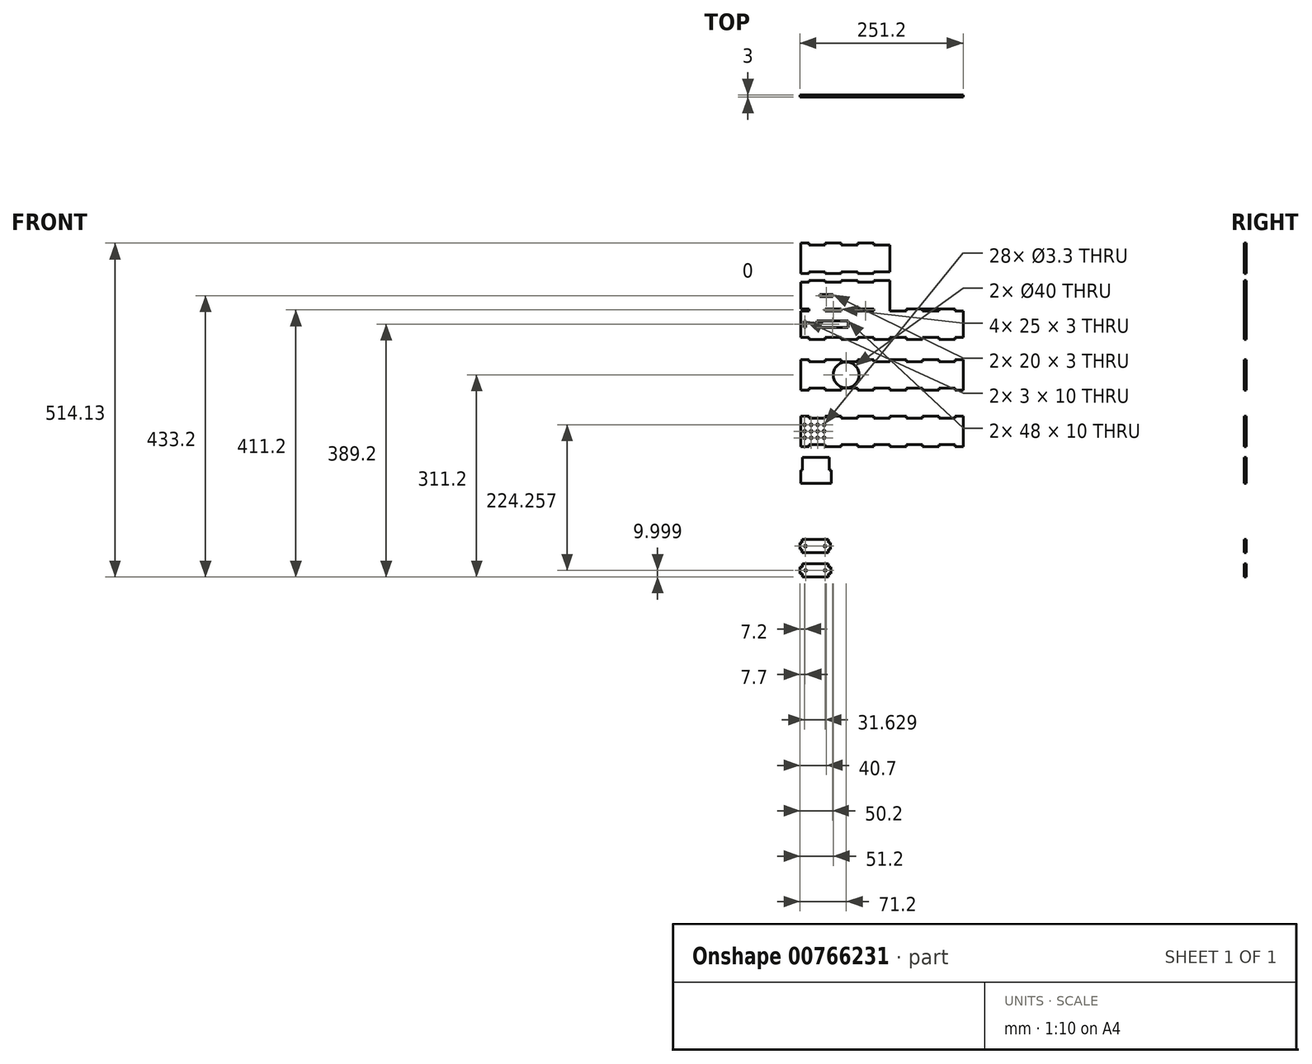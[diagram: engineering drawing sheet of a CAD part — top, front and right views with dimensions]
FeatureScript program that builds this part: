
annotation { "Feature Type Name" : "Feature", "Feature Type Description" : "" }
export const myFeature = defineFeature(function(context is Context, id is Id, definition is map)
    precondition{}
    {
        {
            var Q0;
            Q0=qCreatedBy(makeId("Front.planeOp"),FACE);
            var sketch = newSketch(context, id + "F0", { "sketchPlane" : qUnion([Q0])});
            skLineSegment(sketch, "E0.bottom", {"start": v(-125, 23.5) * mm, "end": v(-112.5, 23.5) * mm});
            skLineSegment(sketch, "E0.top", {"start": v(-125, -23.5) * mm, "end": v(-112.5, -23.5) * mm});
            skLineSegment(sketch, "E0.left", {"start": v(-125, 23.5) * mm, "end": v(-125, -23.5) * mm});
            skLineSegment(sketch, "E0.right", {"start": v(125, 23.5) * mm, "end": v(125, -23.5) * mm});
            skPoint(sketch, "E0.middle", {"position": v(0, 0) * mm});
            skLineSegment(sketch, "E1", {"start": v(-112.5, 23.5) * mm, "end": v(-112.5, 20.5) * mm});
            skLineSegment(sketch, "E2", {"start": v(-112.5, 20.5) * mm, "end": v(-87.5, 20.5) * mm});
            skLineSegment(sketch, "E3", {"start": v(-87.5, 20.5) * mm, "end": v(-87.5, 23.5) * mm});
            skLineSegment(sketch, "E4.1.0.0", {"start": v(-62.5, 23.5) * mm, "end": v(-62.5, 20.5) * mm});
            skLineSegment(sketch, "E4.1.0.1", {"start": v(-62.5, 20.5) * mm, "end": v(-37.5, 20.5) * mm});
            skLineSegment(sketch, "E4.1.0.2", {"start": v(-37.5, 20.5) * mm, "end": v(-37.5, 23.5) * mm});
            skLineSegment(sketch, "E4.2.0.0", {"start": v(-12.5, 23.5) * mm, "end": v(-12.5, 20.5) * mm});
            skLineSegment(sketch, "E4.2.0.1", {"start": v(-12.5, 20.5) * mm, "end": v(12.5, 20.5) * mm});
            skLineSegment(sketch, "E4.2.0.2", {"start": v(12.5, 20.5) * mm, "end": v(12.5, 23.5) * mm});
            skLineSegment(sketch, "E4.3.0.0", {"start": v(37.5, 23.5) * mm, "end": v(37.5, 20.5) * mm});
            skLineSegment(sketch, "E4.3.0.1", {"start": v(37.5, 20.5) * mm, "end": v(62.5, 20.5) * mm});
            skLineSegment(sketch, "E4.3.0.2", {"start": v(62.5, 20.5) * mm, "end": v(62.5, 23.5) * mm});
            skLineSegment(sketch, "E4.4.0.0", {"start": v(87.5, 23.5) * mm, "end": v(87.5, 20.5) * mm});
            skLineSegment(sketch, "E4.4.0.1", {"start": v(87.5, 20.5) * mm, "end": v(112.5, 20.5) * mm});
            skLineSegment(sketch, "E4.4.0.2", {"start": v(112.5, 20.5) * mm, "end": v(112.5, 23.5) * mm});
            skLineSegment(sketch, "E4.direction1", {"start": v(-112.5, 20.5) * mm, "end": v(-62.5, 20.5) * mm, "construction": true});
            skLineSegment(sketch, "E5.trimOffspring", {"start": v(-87.5, 23.5) * mm, "end": v(-62.5, 23.5) * mm});
            skLineSegment(sketch, "E6.trimOffspring", {"start": v(-37.5, 23.5) * mm, "end": v(-12.5, 23.5) * mm});
            skLineSegment(sketch, "E7.trimOffspring", {"start": v(12.5, 23.5) * mm, "end": v(37.5, 23.5) * mm});
            skLineSegment(sketch, "E8.trimOffspring", {"start": v(62.5, 23.5) * mm, "end": v(87.5, 23.5) * mm});
            skLineSegment(sketch, "E9.trimOffspring", {"start": v(112.5, 23.5) * mm, "end": v(125, 23.5) * mm});
            skLineSegment(sketch, "E10", {"start": v(-112.5, -23.5) * mm, "end": v(-112.5, -20.5) * mm});
            skLineSegment(sketch, "E11", {"start": v(-112.5, -20.5) * mm, "end": v(-87.5, -20.5) * mm});
            skLineSegment(sketch, "E12", {"start": v(-87.5, -20.5) * mm, "end": v(-87.5, -23.5) * mm});
            skLineSegment(sketch, "E13.1.0.0", {"start": v(-62.5, -23.5) * mm, "end": v(-62.5, -20.5) * mm});
            skLineSegment(sketch, "E13.1.0.1", {"start": v(-62.5, -20.5) * mm, "end": v(-37.5, -20.5) * mm});
            skLineSegment(sketch, "E13.1.0.2", {"start": v(-37.5, -20.5) * mm, "end": v(-37.5, -23.5) * mm});
            skLineSegment(sketch, "E13.2.0.0", {"start": v(-12.5, -23.5) * mm, "end": v(-12.5, -20.5) * mm});
            skLineSegment(sketch, "E13.2.0.1", {"start": v(-12.5, -20.5) * mm, "end": v(12.5, -20.5) * mm});
            skLineSegment(sketch, "E13.2.0.2", {"start": v(12.5, -20.5) * mm, "end": v(12.5, -23.5) * mm});
            skLineSegment(sketch, "E13.3.0.0", {"start": v(37.5, -23.5) * mm, "end": v(37.5, -20.5) * mm});
            skLineSegment(sketch, "E13.3.0.1", {"start": v(37.5, -20.5) * mm, "end": v(62.5, -20.5) * mm});
            skLineSegment(sketch, "E13.3.0.2", {"start": v(62.5, -20.5) * mm, "end": v(62.5, -23.5) * mm});
            skLineSegment(sketch, "E13.4.0.0", {"start": v(87.5, -23.5) * mm, "end": v(87.5, -20.5) * mm});
            skLineSegment(sketch, "E13.4.0.1", {"start": v(87.5, -20.5) * mm, "end": v(112.5, -20.5) * mm});
            skLineSegment(sketch, "E13.4.0.2", {"start": v(112.5, -20.5) * mm, "end": v(112.5, -23.5) * mm});
            skLineSegment(sketch, "E13.direction1", {"start": v(-87.5, -23.5) * mm, "end": v(-62.5, -23.5) * mm, "construction": true});
            skLineSegment(sketch, "E14.trimOffspring", {"start": v(-37.5, -23.5) * mm, "end": v(-12.5, -23.5) * mm});
            skLineSegment(sketch, "E15.trimOffspring", {"start": v(-87.5, -23.5) * mm, "end": v(-62.5, -23.5) * mm});
            skLineSegment(sketch, "E16.trimOffspring", {"start": v(62.5, -23.5) * mm, "end": v(87.5, -23.5) * mm});
            skLineSegment(sketch, "E17.trimOffspring", {"start": v(12.5, -23.5) * mm, "end": v(37.5, -23.5) * mm});
            skLineSegment(sketch, "E18.trimOffspring", {"start": v(112.5, -23.5) * mm, "end": v(125, -23.5) * mm});
            skLineSegment(sketch, "E19.bottom", {"start": v(-112.5, 145.5) * mm, "end": v(-87.5, 145.5) * mm});
            skLineSegment(sketch, "E19.top", {"start": v(-112.5, 54.5) * mm, "end": v(-87.5, 54.5) * mm});
            skLineSegment(sketch, "E19.left", {"start": v(-125, 142.5) * mm, "end": v(-125, 101.5) * mm});
            skPoint(sketch, "E19.middle", {"position": v(0, 100) * mm});
            skLineSegment(sketch, "E20", {"start": v(-125, 57.5) * mm, "end": v(-112.5, 57.5) * mm});
            skLineSegment(sketch, "E21", {"start": v(-112.5, 57.5) * mm, "end": v(-112.5, 54.5) * mm});
            skLineSegment(sketch, "E22", {"start": v(-87.5, 54.5) * mm, "end": v(-87.5, 57.5) * mm});
            skLineSegment(sketch, "E23", {"start": v(-87.5, 57.5) * mm, "end": v(-62.5, 57.5) * mm});
            skLineSegment(sketch, "E24", {"start": v(-62.5, 57.5) * mm, "end": v(-62.5, 54.5) * mm});
            skLineSegment(sketch, "E25.1.0.0", {"start": v(-37.5, 54.5) * mm, "end": v(-37.5, 57.5) * mm});
            skLineSegment(sketch, "E25.1.0.1", {"start": v(-37.5, 57.5) * mm, "end": v(-12.5, 57.5) * mm});
            skLineSegment(sketch, "E25.1.0.2", {"start": v(-12.5, 57.5) * mm, "end": v(-12.5, 54.5) * mm});
            skLineSegment(sketch, "E25.2.0.0", {"start": v(12.5, 54.5) * mm, "end": v(12.5, 57.5) * mm});
            skLineSegment(sketch, "E25.2.0.1", {"start": v(12.5, 57.5) * mm, "end": v(37.5, 57.5) * mm});
            skLineSegment(sketch, "E25.2.0.2", {"start": v(37.5, 57.5) * mm, "end": v(37.5, 54.5) * mm});
            skLineSegment(sketch, "E25.3.0.0", {"start": v(62.5, 54.5) * mm, "end": v(62.5, 57.5) * mm});
            skLineSegment(sketch, "E25.3.0.1", {"start": v(62.5, 57.5) * mm, "end": v(87.5, 57.5) * mm});
            skLineSegment(sketch, "E25.3.0.2", {"start": v(87.5, 57.5) * mm, "end": v(87.5, 54.5) * mm});
            skLineSegment(sketch, "E25.direction1", {"start": v(-62.5, 54.5) * mm, "end": v(-37.5, 54.5) * mm, "construction": true});
            skLineSegment(sketch, "E26", {"start": v(112.5, 54.5) * mm, "end": v(112.5, 57.5) * mm});
            skLineSegment(sketch, "E27", {"start": v(112.5, 57.5) * mm, "end": v(125, 57.5) * mm});
            skPoint(sketch, "E28.orphan", {"position": v(125, 54.5) * mm});
            skLineSegment(sketch, "E29.trimOffspring", {"start": v(87.5, 54.5) * mm, "end": v(112.5, 54.5) * mm});
            skLineSegment(sketch, "E30.trimOffspring", {"start": v(37.5, 54.5) * mm, "end": v(62.5, 54.5) * mm});
            skLineSegment(sketch, "E31.trimOffspring", {"start": v(-12.5, 54.5) * mm, "end": v(12.5, 54.5) * mm});
            skPoint(sketch, "E32.orphan", {"position": v(-125, 54.5) * mm});
            skLineSegment(sketch, "E33.trimOffspring", {"start": v(-62.5, 54.5) * mm, "end": v(-37.5, 54.5) * mm});
            skLineSegment(sketch, "E34", {"start": v(-125, 142.5) * mm, "end": v(-112.5, 142.5) * mm});
            skLineSegment(sketch, "E35", {"start": v(-112.5, 142.5) * mm, "end": v(-112.5, 145.5) * mm});
            skLineSegment(sketch, "E36", {"start": v(-87.5, 145.5) * mm, "end": v(-87.5, 142.5) * mm});
            skLineSegment(sketch, "E37", {"start": v(-87.5, 142.5) * mm, "end": v(-62.5, 142.5) * mm});
            skLineSegment(sketch, "E38", {"start": v(-62.5, 142.5) * mm, "end": v(-62.5, 145.5) * mm});
            skLineSegment(sketch, "E39.1.0.0", {"start": v(-37.5, 145.5) * mm, "end": v(-37.5, 142.5) * mm});
            skLineSegment(sketch, "E39.1.0.1", {"start": v(-37.5, 142.5) * mm, "end": v(-12.5, 142.5) * mm});
            skLineSegment(sketch, "E39.1.0.2", {"start": v(-12.5, 142.5) * mm, "end": v(-12.5, 145.5) * mm});
            skLineSegment(sketch, "E39.2.0.0", {"start": v(12.5, 145.5) * mm, "end": v(12.5, 142.5) * mm});
            skLineSegment(sketch, "E39.direction1", {"start": v(-87.5, 142.5) * mm, "end": v(-37.5, 142.5) * mm, "construction": true});
            skPoint(sketch, "E40.orphan", {"position": v(-125, 145.5) * mm});
            skLineSegment(sketch, "E41.trimOffspring", {"start": v(-62.5, 145.5) * mm, "end": v(-37.5, 145.5) * mm});
            skLineSegment(sketch, "E42.trimOffspring", {"start": v(-12.5, 145.5) * mm, "end": v(12.5, 145.5) * mm});
            skLineSegment(sketch, "E43.bottom", {"start": v(-62.5, 98.5) * mm, "end": v(-87.5, 98.5) * mm});
            skLineSegment(sketch, "E43.top", {"start": v(-62.5, 101.5) * mm, "end": v(-87.5, 101.5) * mm});
            skLineSegment(sketch, "E43.left", {"start": v(-62.5, 98.5) * mm, "end": v(-62.5, 101.5) * mm});
            skLineSegment(sketch, "E43.right", {"start": v(-87.5, 98.5) * mm, "end": v(-87.5, 101.5) * mm});
            skPoint(sketch, "E43.middle", {"position": v(-75, 100) * mm});
            skPoint(sketch, "E44.1.0.0", {"position": v(-25, 100) * mm});
            skLineSegment(sketch, "E44.1.0.1", {"start": v(-12.5, 101.5) * mm, "end": v(-37.5, 101.5) * mm});
            skLineSegment(sketch, "E44.1.0.2", {"start": v(-12.5, 98.5) * mm, "end": v(-37.5, 98.5) * mm});
            skLineSegment(sketch, "E44.1.0.3", {"start": v(-12.5, 98.5) * mm, "end": v(-12.5, 101.5) * mm});
            skLineSegment(sketch, "E44.1.0.4", {"start": v(-37.5, 98.5) * mm, "end": v(-37.5, 101.5) * mm});
            skPoint(sketch, "E44.2.0.0", {"position": v(25, 100) * mm});
            skLineSegment(sketch, "E44.2.0.2", {"start": v(37.5, 98.5) * mm, "end": v(12.5, 98.5) * mm});
            skLineSegment(sketch, "E44.2.0.3", {"start": v(37.5, 98.5) * mm, "end": v(37.5, 101.5) * mm});
            skLineSegment(sketch, "E44.2.0.4", {"start": v(12.5, 98.5) * mm, "end": v(12.5, 101.5) * mm});
            skPoint(sketch, "E44.3.0.0", {"position": v(75, 100) * mm});
            skLineSegment(sketch, "E44.3.0.2", {"start": v(87.5, 98.5) * mm, "end": v(62.5, 98.5) * mm});
            skLineSegment(sketch, "E44.3.0.3", {"start": v(87.5, 98.5) * mm, "end": v(87.5, 101.5) * mm});
            skLineSegment(sketch, "E44.3.0.4", {"start": v(62.5, 98.5) * mm, "end": v(62.5, 101.5) * mm});
            skLineSegment(sketch, "E44.direction1", {"start": v(-87.5, 98.5) * mm, "end": v(-37.5, 98.5) * mm, "construction": true});
            skLineSegment(sketch, "E45", {"start": v(-125, 101.5) * mm, "end": v(-112.5, 101.5) * mm});
            skLineSegment(sketch, "E46", {"start": v(-112.5, 101.5) * mm, "end": v(-112.5, 98.5) * mm});
            skLineSegment(sketch, "E47", {"start": v(-112.5, 98.5) * mm, "end": v(-125, 98.5) * mm});
            skLineSegment(sketch, "E48", {"start": v(112.5, 101.5) * mm, "end": v(112.5, 98.5) * mm});
            skLineSegment(sketch, "E49", {"start": v(112.5, 98.5) * mm, "end": v(125, 98.5) * mm});
            skLineSegment(sketch, "E50.trimOffspring", {"start": v(125, 98.5) * mm, "end": v(125, 57.5) * mm});
            skLineSegment(sketch, "E51.trimOffspring", {"start": v(-125, 98.5) * mm, "end": v(-125, 57.5) * mm});
            skLineSegment(sketch, "E52", {"start": v(112.5, 101.5) * mm, "end": v(37.5, 101.5) * mm});
            skLineSegment(sketch, "E53", {"start": v(12.5, 101.5) * mm, "end": v(12.5, 142.5) * mm});
            skPoint(sketch, "E54.start.orphan", {"position": v(125, 101.5) * mm});
            skLineSegment(sketch, "E55.bottom", {"start": v(-125, 202.93) * mm, "end": v(-112.5, 202.93) * mm});
            skLineSegment(sketch, "E55.top", {"start": v(-125, 155.93) * mm, "end": v(-112.5, 155.93) * mm});
            skLineSegment(sketch, "E55.left", {"start": v(-125, 202.93) * mm, "end": v(-125, 155.93) * mm});
            skPoint(sketch, "E55.middle", {"position": v(0, 179.43) * mm});
            skLineSegment(sketch, "E56", {"start": v(-112.5, 202.93) * mm, "end": v(-112.5, 199.93) * mm});
            skLineSegment(sketch, "E57", {"start": v(-112.5, 199.93) * mm, "end": v(-87.5, 199.93) * mm});
            skLineSegment(sketch, "E58", {"start": v(-87.5, 199.93) * mm, "end": v(-87.5, 202.93) * mm});
            skLineSegment(sketch, "E59.1.0.0", {"start": v(-62.5, 202.93) * mm, "end": v(-62.5, 199.93) * mm});
            skLineSegment(sketch, "E59.1.0.1", {"start": v(-62.5, 199.93) * mm, "end": v(-37.5, 199.93) * mm});
            skLineSegment(sketch, "E59.1.0.2", {"start": v(-37.5, 199.93) * mm, "end": v(-37.5, 202.93) * mm});
            skLineSegment(sketch, "E59.2.0.0", {"start": v(-12.5, 202.93) * mm, "end": v(-12.5, 199.93) * mm});
            skLineSegment(sketch, "E59.2.0.1", {"start": v(-12.5, 199.93) * mm, "end": v(12.5, 199.93) * mm});
            skLineSegment(sketch, "E59.direction1", {"start": v(-112.5, 199.93) * mm, "end": v(-62.5, 199.93) * mm, "construction": true});
            skLineSegment(sketch, "E60.trimOffspring", {"start": v(-87.5, 202.93) * mm, "end": v(-62.5, 202.93) * mm});
            skLineSegment(sketch, "E61.trimOffspring", {"start": v(-37.5, 202.93) * mm, "end": v(-12.5, 202.93) * mm});
            skLineSegment(sketch, "E62", {"start": v(-112.5, 155.93) * mm, "end": v(-112.5, 158.93) * mm});
            skLineSegment(sketch, "E63", {"start": v(-112.5, 158.93) * mm, "end": v(-87.5, 158.93) * mm});
            skLineSegment(sketch, "E64", {"start": v(-87.5, 158.93) * mm, "end": v(-87.5, 155.93) * mm});
            skLineSegment(sketch, "E65.1.0.0", {"start": v(-62.5, 155.93) * mm, "end": v(-62.5, 158.93) * mm});
            skLineSegment(sketch, "E65.1.0.1", {"start": v(-62.5, 158.93) * mm, "end": v(-37.5, 158.93) * mm});
            skLineSegment(sketch, "E65.1.0.2", {"start": v(-37.5, 158.93) * mm, "end": v(-37.5, 155.93) * mm});
            skLineSegment(sketch, "E65.2.0.0", {"start": v(-12.5, 155.93) * mm, "end": v(-12.5, 158.93) * mm});
            skLineSegment(sketch, "E65.2.0.1", {"start": v(-12.5, 158.93) * mm, "end": v(12.5, 158.93) * mm});
            skLineSegment(sketch, "E65.direction1", {"start": v(-87.5, 155.93) * mm, "end": v(-62.5, 155.93) * mm, "construction": true});
            skLineSegment(sketch, "E66.trimOffspring", {"start": v(-37.5, 155.93) * mm, "end": v(-12.5, 155.93) * mm});
            skLineSegment(sketch, "E67.trimOffspring", {"start": v(-87.5, 155.93) * mm, "end": v(-62.5, 155.93) * mm});
            skLineSegment(sketch, "E68", {"start": v(12.5, 199.93) * mm, "end": v(12.5, 158.93) * mm});
            skLineSegment(sketch, "E69.bottom", {"start": v(-125, -63.44) * mm, "end": v(-112.5, -63.44) * mm});
            skLineSegment(sketch, "E69.top", {"start": v(-125, -110.44) * mm, "end": v(-112.5, -110.44) * mm});
            skLineSegment(sketch, "E69.left", {"start": v(-125, -63.44) * mm, "end": v(-125, -110.44) * mm});
            skLineSegment(sketch, "E69.right", {"start": v(125, -63.44) * mm, "end": v(125, -110.44) * mm});
            skPoint(sketch, "E69.middle", {"position": v(0, -86.94) * mm});
            skLineSegment(sketch, "E70", {"start": v(-112.5, -63.44) * mm, "end": v(-112.5, -66.44) * mm});
            skLineSegment(sketch, "E71", {"start": v(-112.5, -66.44) * mm, "end": v(-87.5, -66.44) * mm});
            skLineSegment(sketch, "E72", {"start": v(-87.5, -66.44) * mm, "end": v(-87.5, -63.44) * mm});
            skLineSegment(sketch, "E73.1.0.0", {"start": v(-62.5, -63.44) * mm, "end": v(-62.5, -66.44) * mm});
            skLineSegment(sketch, "E73.1.0.1", {"start": v(-62.5, -66.44) * mm, "end": v(-37.5, -66.44) * mm});
            skLineSegment(sketch, "E73.1.0.2", {"start": v(-37.5, -66.44) * mm, "end": v(-37.5, -63.44) * mm});
            skLineSegment(sketch, "E73.2.0.0", {"start": v(-12.5, -63.44) * mm, "end": v(-12.5, -66.44) * mm});
            skLineSegment(sketch, "E73.2.0.1", {"start": v(-12.5, -66.44) * mm, "end": v(12.5, -66.44) * mm});
            skLineSegment(sketch, "E73.2.0.2", {"start": v(12.5, -66.44) * mm, "end": v(12.5, -63.44) * mm});
            skLineSegment(sketch, "E73.3.0.0", {"start": v(37.5, -63.44) * mm, "end": v(37.5, -66.44) * mm});
            skLineSegment(sketch, "E73.3.0.1", {"start": v(37.5, -66.44) * mm, "end": v(62.5, -66.44) * mm});
            skLineSegment(sketch, "E73.3.0.2", {"start": v(62.5, -66.44) * mm, "end": v(62.5, -63.44) * mm});
            skLineSegment(sketch, "E73.4.0.0", {"start": v(87.5, -63.44) * mm, "end": v(87.5, -66.44) * mm});
            skLineSegment(sketch, "E73.4.0.1", {"start": v(87.5, -66.44) * mm, "end": v(112.5, -66.44) * mm});
            skLineSegment(sketch, "E73.4.0.2", {"start": v(112.5, -66.44) * mm, "end": v(112.5, -63.44) * mm});
            skLineSegment(sketch, "E73.direction1", {"start": v(-112.5, -66.44) * mm, "end": v(-62.5, -66.44) * mm, "construction": true});
            skLineSegment(sketch, "E74.trimOffspring", {"start": v(-87.5, -63.44) * mm, "end": v(-62.5, -63.44) * mm});
            skLineSegment(sketch, "E75.trimOffspring", {"start": v(-37.5, -63.44) * mm, "end": v(-12.5, -63.44) * mm});
            skLineSegment(sketch, "E76.trimOffspring", {"start": v(12.5, -63.44) * mm, "end": v(37.5, -63.44) * mm});
            skLineSegment(sketch, "E77.trimOffspring", {"start": v(62.5, -63.44) * mm, "end": v(87.5, -63.44) * mm});
            skLineSegment(sketch, "E78.trimOffspring", {"start": v(112.5, -63.44) * mm, "end": v(125, -63.44) * mm});
            skLineSegment(sketch, "E79", {"start": v(-112.5, -110.44) * mm, "end": v(-112.5, -107.44) * mm});
            skLineSegment(sketch, "E80", {"start": v(-112.5, -107.44) * mm, "end": v(-87.5, -107.44) * mm});
            skLineSegment(sketch, "E81", {"start": v(-87.5, -107.44) * mm, "end": v(-87.5, -110.44) * mm});
            skLineSegment(sketch, "E82.1.0.0", {"start": v(-62.5, -110.44) * mm, "end": v(-62.5, -107.44) * mm});
            skLineSegment(sketch, "E82.1.0.1", {"start": v(-62.5, -107.44) * mm, "end": v(-37.5, -107.44) * mm});
            skLineSegment(sketch, "E82.1.0.2", {"start": v(-37.5, -107.44) * mm, "end": v(-37.5, -110.44) * mm});
            skLineSegment(sketch, "E82.2.0.0", {"start": v(-12.5, -110.44) * mm, "end": v(-12.5, -107.44) * mm});
            skLineSegment(sketch, "E82.2.0.1", {"start": v(-12.5, -107.44) * mm, "end": v(12.5, -107.44) * mm});
            skLineSegment(sketch, "E82.2.0.2", {"start": v(12.5, -107.44) * mm, "end": v(12.5, -110.44) * mm});
            skLineSegment(sketch, "E82.3.0.0", {"start": v(37.5, -110.44) * mm, "end": v(37.5, -107.44) * mm});
            skLineSegment(sketch, "E82.3.0.1", {"start": v(37.5, -107.44) * mm, "end": v(62.5, -107.44) * mm});
            skLineSegment(sketch, "E82.3.0.2", {"start": v(62.5, -107.44) * mm, "end": v(62.5, -110.44) * mm});
            skLineSegment(sketch, "E82.4.0.0", {"start": v(87.5, -110.44) * mm, "end": v(87.5, -107.44) * mm});
            skLineSegment(sketch, "E82.4.0.1", {"start": v(87.5, -107.44) * mm, "end": v(112.5, -107.44) * mm});
            skLineSegment(sketch, "E82.4.0.2", {"start": v(112.5, -107.44) * mm, "end": v(112.5, -110.44) * mm});
            skLineSegment(sketch, "E82.direction1", {"start": v(-87.5, -110.44) * mm, "end": v(-62.5, -110.44) * mm, "construction": true});
            skLineSegment(sketch, "E83.trimOffspring", {"start": v(-37.5, -110.44) * mm, "end": v(-12.5, -110.44) * mm});
            skLineSegment(sketch, "E84.trimOffspring", {"start": v(-87.5, -110.44) * mm, "end": v(-62.5, -110.44) * mm});
            skLineSegment(sketch, "E85.trimOffspring", {"start": v(62.5, -110.44) * mm, "end": v(87.5, -110.44) * mm});
            skLineSegment(sketch, "E86.trimOffspring", {"start": v(12.5, -110.44) * mm, "end": v(37.5, -110.44) * mm});
            skLineSegment(sketch, "E87.trimOffspring", {"start": v(112.5, -110.44) * mm, "end": v(125, -110.44) * mm});
            skCircle(sketch, "E88", {"center": v(-55, 0) * mm, "radius": 20 * mm});
            skLineSegment(sketch, "E89.bottom", {"start": v(-100, 73) * mm, "end": v(-52, 73) * mm});
            skLineSegment(sketch, "E89.top", {"start": v(-100, 83) * mm, "end": v(-52, 83) * mm});
            skLineSegment(sketch, "E89.left", {"start": v(-100, 73) * mm, "end": v(-100, 83) * mm});
            skLineSegment(sketch, "E89.right", {"start": v(-52, 73) * mm, "end": v(-52, 83) * mm});
            skLineSegment(sketch, "E90.bottom", {"start": v(-95.5, 123.5) * mm, "end": v(-75.5, 123.5) * mm});
            skLineSegment(sketch, "E90.top", {"start": v(-95.5, 120.5) * mm, "end": v(-75.5, 120.5) * mm});
            skLineSegment(sketch, "E90.left", {"start": v(-95.5, 123.5) * mm, "end": v(-95.5, 120.5) * mm});
            skLineSegment(sketch, "E90.right", {"start": v(-75.5, 123.5) * mm, "end": v(-75.5, 120.5) * mm});
            skCircle(sketch, "E91", {"center": v(-119, -86.94) * mm, "radius": 1.65 * mm});
            skCircle(sketch, "E92.1.0.0", {"center": v(-109, -86.94) * mm, "radius": 1.65 * mm});
            skCircle(sketch, "E92.2.0.0", {"center": v(-99, -86.94) * mm, "radius": 1.65 * mm});
            skCircle(sketch, "E92.3.0.0", {"center": v(-89, -86.94) * mm, "radius": 1.65 * mm});
            skLineSegment(sketch, "E92.direction1", {"start": v(-119, -86.94) * mm, "end": v(-109, -86.94) * mm, "construction": true});
            skCircle(sketch, "E93", {"center": v(-119, -76.94) * mm, "radius": 1.65 * mm});
            skCircle(sketch, "E94", {"center": v(-119, -96.94) * mm, "radius": 1.65 * mm});
            skCircle(sketch, "E95.1.0.0", {"center": v(-109, -76.94) * mm, "radius": 1.65 * mm});
            skCircle(sketch, "E95.1.0.1", {"center": v(-109, -96.94) * mm, "radius": 1.65 * mm});
            skCircle(sketch, "E95.2.0.0", {"center": v(-99, -76.94) * mm, "radius": 1.65 * mm});
            skCircle(sketch, "E95.2.0.1", {"center": v(-99, -96.94) * mm, "radius": 1.65 * mm});
            skCircle(sketch, "E95.3.0.0", {"center": v(-89, -76.94) * mm, "radius": 1.65 * mm});
            skCircle(sketch, "E95.3.0.1", {"center": v(-89, -96.94) * mm, "radius": 1.65 * mm});
            skLineSegment(sketch, "E95.direction1", {"start": v(-119, -76.94) * mm, "end": v(-109, -76.94) * mm, "construction": true});
            skLineSegment(sketch, "E96.bottom", {"start": v(-125.12, -146.8) * mm, "end": v(-122.12, -146.8) * mm});
            skLineSegment(sketch, "E96.top", {"start": v(-125.12, -166.8) * mm, "end": v(-78.12, -166.8) * mm});
            skLineSegment(sketch, "E96.left", {"start": v(-125.12, -146.8) * mm, "end": v(-125.12, -166.8) * mm});
            skLineSegment(sketch, "E96.right", {"start": v(-78.12, -146.8) * mm, "end": v(-78.12, -166.8) * mm});
            skLineSegment(sketch, "E97.bottom", {"start": v(-125.87, -306.2) * mm, "end": v(-122.37, -306.2) * mm});
            skLineSegment(sketch, "E97.top", {"start": v(-125.87, -296.2) * mm, "end": v(-122.37, -296.2) * mm});
            skLineSegment(sketch, "E97.left", {"start": v(-125.87, -306.2) * mm, "end": v(-125.87, -296.2) * mm});
            skLineSegment(sketch, "E97.right", {"start": v(-78.87, -306.2) * mm, "end": v(-78.87, -296.2) * mm});
            skLineSegment(sketch, "E98.top", {"start": v(-122.12, -126.8) * mm, "end": v(-81.12, -126.8) * mm});
            skLineSegment(sketch, "E98.left", {"start": v(-122.12, -146.8) * mm, "end": v(-122.12, -126.8) * mm});
            skLineSegment(sketch, "E98.right", {"start": v(-81.12, -146.8) * mm, "end": v(-81.12, -126.8) * mm});
            skLineSegment(sketch, "E99.trimOffspring", {"start": v(-81.12, -146.8) * mm, "end": v(-78.12, -146.8) * mm});
            skLineSegment(sketch, "E100.bottom", {"start": v(-122.37, -291.2) * mm, "end": v(-82.37, -291.2) * mm});
            skLineSegment(sketch, "E100.top", {"start": v(-122.37, -311.2) * mm, "end": v(-82.37, -311.2) * mm});
            skLineSegment(sketch, "E100.left", {"start": v(-122.37, -291.2) * mm, "end": v(-122.37, -296.2) * mm});
            skLineSegment(sketch, "E100.right", {"start": v(-82.37, -291.2) * mm, "end": v(-82.37, -296.2) * mm});
            skLineSegment(sketch, "E101.trimOffspring", {"start": v(-122.37, -306.2) * mm, "end": v(-122.37, -311.2) * mm});
            skLineSegment(sketch, "E102.trimOffspring", {"start": v(-82.37, -296.2) * mm, "end": v(-78.87, -296.2) * mm});
            skLineSegment(sketch, "E103.trimOffspring", {"start": v(-82.37, -306.2) * mm, "end": v(-78.87, -306.2) * mm});
            skLineSegment(sketch, "E104.trimOffspring", {"start": v(-82.37, -306.2) * mm, "end": v(-82.37, -311.2) * mm});
            skCircle(sketch, "E105", {"center": v(-117.37, -301.2) * mm, "radius": 1.65 * mm});
            skCircle(sketch, "E106", {"center": v(-87.37, -301.2) * mm, "radius": 1.65 * mm});
            skLineSegment(sketch, "E107.bottom", {"start": v(-120, 83) * mm, "end": v(-117, 83) * mm});
            skLineSegment(sketch, "E107.top", {"start": v(-120, 73) * mm, "end": v(-117, 73) * mm});
            skLineSegment(sketch, "E107.left", {"start": v(-120, 83) * mm, "end": v(-120, 73) * mm});
            skLineSegment(sketch, "E107.right", {"start": v(-117, 83) * mm, "end": v(-117, 73) * mm});
            skLineSegment(sketch, "E108.bottom", {"start": v(-126.2, -268.73) * mm, "end": v(-123.2, -268.73) * mm});
            skLineSegment(sketch, "E108.top", {"start": v(-126.2, -258.73) * mm, "end": v(-123.2, -258.73) * mm});
            skLineSegment(sketch, "E108.left", {"start": v(-126.2, -268.73) * mm, "end": v(-126.2, -258.73) * mm});
            skLineSegment(sketch, "E108.right", {"start": v(-79.2, -268.73) * mm, "end": v(-79.2, -258.73) * mm});
            skLineSegment(sketch, "E109.bottom", {"start": v(-123.2, -253.73) * mm, "end": v(-82.2, -253.73) * mm});
            skLineSegment(sketch, "E109.top", {"start": v(-123.2, -273.73) * mm, "end": v(-82.2, -273.73) * mm});
            skLineSegment(sketch, "E109.left", {"start": v(-123.2, -253.73) * mm, "end": v(-123.2, -258.73) * mm});
            skLineSegment(sketch, "E109.right", {"start": v(-82.2, -253.73) * mm, "end": v(-82.2, -258.73) * mm});
            skLineSegment(sketch, "E110.trimOffspring", {"start": v(-123.2, -268.73) * mm, "end": v(-123.2, -273.73) * mm});
            skLineSegment(sketch, "E111.trimOffspring", {"start": v(-82.2, -258.73) * mm, "end": v(-79.2, -258.73) * mm});
            skLineSegment(sketch, "E112.trimOffspring", {"start": v(-82.2, -268.73) * mm, "end": v(-79.2, -268.73) * mm});
            skLineSegment(sketch, "E113.trimOffspring", {"start": v(-82.2, -268.73) * mm, "end": v(-82.2, -273.73) * mm});
            skCircle(sketch, "E114", {"center": v(-117.7, -263.73) * mm, "radius": 1.65 * mm});
            skCircle(sketch, "E115", {"center": v(-87.7, -263.73) * mm, "radius": 1.65 * mm});
            skSolve(sketch);
        }
        {
            var Q0;
            Q0=makeQuery(id+"F0.imprint","IMPRINT",FACE,{"disambiguationData":[TD([[makeQuery(id+"F0.imprint","IMPRINT",EDGE,{"derivedFrom":sQuery(id+"F0.wireOp",EDGE,"E55.bottom")}),-1.0]])]});
            var Q1;
            Q1=makeQuery(id+"F0.imprint","IMPRINT",FACE,{"disambiguationData":[TD([[makeQuery(id+"F0.imprint","IMPRINT",EDGE,{"derivedFrom":sQuery(id+"F0.wireOp",EDGE,"E19.bottom")}),-1.0]])]});
            var Q2;
            Q2=makeQuery(id+"F0.imprint","IMPRINT",FACE,{"disambiguationData":[TD([[makeQuery(id+"F0.imprint","IMPRINT",EDGE,{"derivedFrom":sQuery(id+"F0.wireOp",EDGE,"E0.right")}),-1.0]])]});
            var Q3;
            Q3=makeQuery(id+"F0.imprint","IMPRINT",FACE,{"disambiguationData":[TD([[makeQuery(id+"F0.imprint","IMPRINT",EDGE,{"derivedFrom":sQuery(id+"F0.wireOp",EDGE,"E0.bottom")}),-1.0]])]});
            var Q4;
            Q4=makeQuery(id+"F0.imprint","IMPRINT",FACE,{"disambiguationData":[TD([[makeQuery(id+"F0.imprint","IMPRINT",EDGE,{"derivedFrom":sQuery(id+"F0.wireOp",EDGE,"E69.bottom")}),-1.0]])]});
            extrude(context, id + "F1", {"entities" : qUnion([Q0, Q1, Q2, Q3, Q4]), "depth" : 3 * mm, "offsetDistance" : 25 * mm});
        }
        {
            var Q0;
            Q0 = qSketchRegion(id + "F0", true);
            extrude(context, id + "F2", {"entities" : qUnion([Q0]), "depth" : 3 * mm, "offsetDistance" : 25 * mm});
        }
    });
